annotation { "Feature Type Name" : "Feature", "Feature Type Description" : "" }
export const myFeature = defineFeature(function(context is Context, id is Id, definition is map)
    precondition{}
    {
        {
            var Q0;
            Q0=qCreatedBy(makeId("Front.planeOp"),FACE);
            var sketch = newSketch(context, id + "F0", { "sketchPlane" : qUnion([Q0])});
            skText(sketch, "E0", { "text": "James\n", "fontName": "RobotoSlab-Bold.ttf"});
            skText(sketch, "E1", { "text": "Sonia Helen", "fontName": "RobotoSlab-Bold.ttf"});
            skText(sketch, "E2", { "text": "Hector", "fontName": "RobotoSlab-Bold.ttf"});
            skText(sketch, "E3", { "text": "Alec\n", "fontName": "RobotoSlab-Bold.ttf"});
            skText(sketch, "E4", { "text": "Xochitl", "fontName": "RobotoSlab-Bold.ttf"});
            skText(sketch, "E5", { "text": "Lourdes", "fontName": "RobotoSlab-Bold.ttf"});
            skText(sketch, "E6", { "text": "John Robert", "fontName": "RobotoSlab-Bold.ttf"});
            const initialGuessF0  = {"E0": [0.00184, 0.00987, 0, 1, 0.004], "E1": [0.01116, 0.00597, 0.7071, 0.7071, 0.004], "E2": [0.01359, -0.00165, 1, 0, 0.004], "E3": [0.00834, -0.01157, 0.7071, -0.7071, 0.004], "E4": [-0.00167, -0.00893, 0, -1, 0.004], "E5": [-0.02327, -0.02624, 0.7071, 0.7071, 0.004], "E6": [-0.0338, -0.00165, 1, 0, 0.004]};
            skSetInitialGuess(sketch, initialGuessF0);
            skSolve(sketch);
        }
        {
            var Q0;
            Q0 = qSketchRegion(id + "F0", true);
            extrude(context, id + "F1", {"entities" : qUnion([Q0]), "depth" : .1 * mm, "offsetDistance" : 25 * mm});
        }
    });